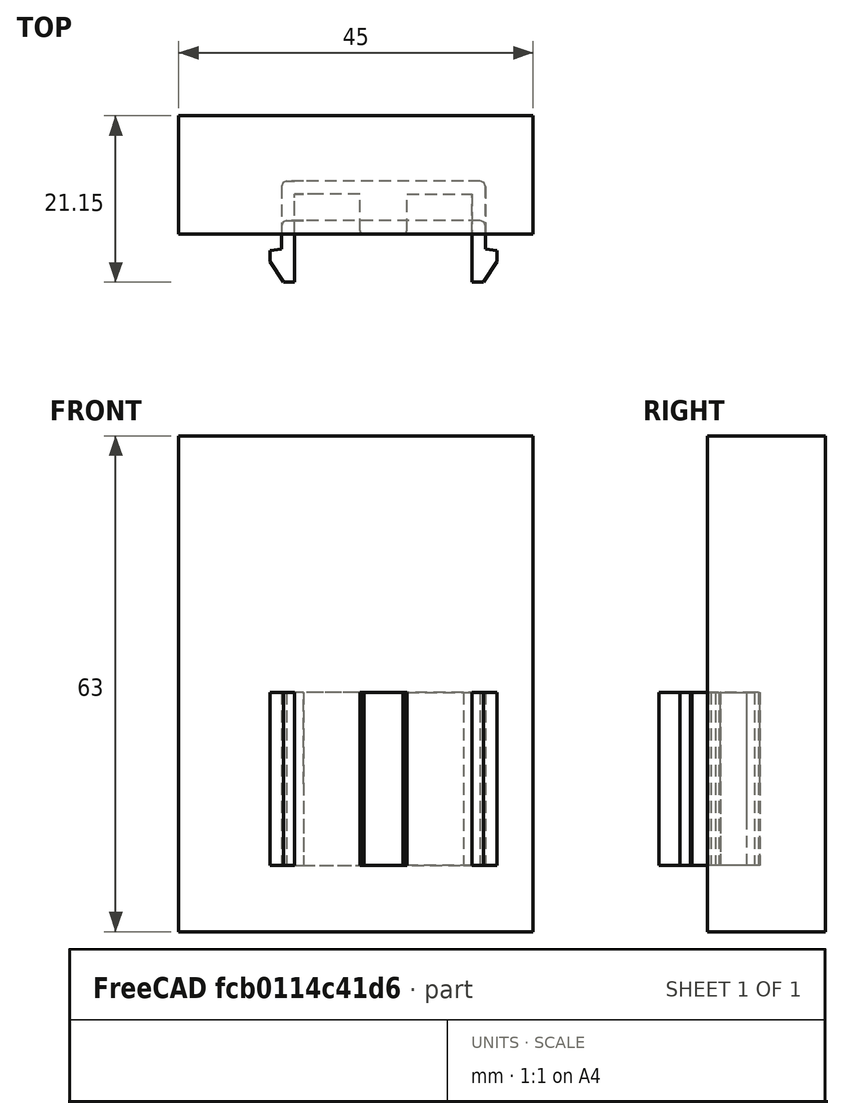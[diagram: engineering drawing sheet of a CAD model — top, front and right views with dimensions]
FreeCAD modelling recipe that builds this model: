
FCSTD DOCUMENT  (FreeCAD 0.17R13541 (Git))
Label: final-extrusion-center-mounter
License: All rights reserved
LicenseURL: http://en.wikipedia.org/wiki/All_rights_reserved
objects: Part::Feature×7, Part::Box×4, Part::MultiCommon×2, Mesh::Feature×1, Part::Cut×1, Part::MultiFuse×1
note: 15 computed .brp shape members not serialized (recipe doc carries the construction recipe); baked Part::Feature solids carry a one-line shape summary decoded from their .brp

FEATURE [Mesh::Feature] cableChain_40MountTop_v2
FEATURE [Part::Feature] cableChain_40MountTop_v2001
  shape: bbox 28.86 x 27.05 x 22 mm, 1492 faces, 0 solids (baked)
FEATURE [Part::Feature] cableChain_40MountTop_v2001_solid  label="cableChain_40MountTop_v2001 (Solid)"
  shape: bbox 28.86 x 27.05 x 22 mm, 1492 faces (baked)
FEATURE [Part::Box] Box  label="Cube"
  AttacherType = Attacher::AttachEngine3D
  Height = 33
  Length = 59
  Placement = pos=(-165.7,-23.2,-95.1) rot=(0,0,1;0rad)
  Width = 31
FEATURE [Part::Feature] cableChain_40MountTop_v2001_solid001  label="cableChain_40MountTop_v2001 (Solid)001"
  shape: bbox 28.86 x 27.05 x 22 mm, 229 faces (baked)
FEATURE [Part::Cut] Cut
  Base = -> cableChain_40MountTop_v2001_solid001
  Tool = -> Box
FEATURE [Part::Box] Box001  label="Cube001"
  AttacherType = Attacher::AttachEngine3D
  Height = 63
  Length = 45
  Placement = pos=(-171,-29.9,-98.4) rot=(0,0,1;0rad)
  Width = 15
FEATURE [Part::Feature] Cut_solid  label="Cut (Solid)"
  shape: bbox 28.86 x 15.02 x 22 mm, 47 faces (baked)
FEATURE [Part::Feature] Cut_solid001  label="Cut (Solid)001"
  shape: bbox 28.86 x 15.02 x 22 mm, 47 faces (baked)
FEATURE [Part::Box] Box002  label="Cube002"
  AttacherType = Attacher::AttachEngine3D
  Height = 63
  Length = 45
  Placement = pos=(-171,-36.9,-98.4) rot=(0,0,1;0rad)
  Width = 7
FEATURE [Part::Box] Box003  label="Cube003"
  AttacherType = Attacher::AttachEngine3D
  Height = 63
  Length = 45
  Placement = pos=(-171,-24.9,-98.4) rot=(0,0,1;0rad)
  Width = 5
FEATURE [Part::MultiCommon] Common
  Placement = pos=(0,-5,0) rot=(0,0,1;0rad)
  Shapes = -> [Box003,Cut_solid001]
FEATURE [Part::MultiCommon] Common001
  Shapes = -> [Cut_solid,Box002]
FEATURE [Part::MultiFuse] Fusion
  Shapes = -> [Common,Common001]
FEATURE [Part::Feature] Fusion001
  shape: bbox 28.86 x 7.85 x 22 mm, 47 faces (baked)
FEATURE [Part::Feature] Fusion_solid  label="Fusion (Solid)"
  shape: bbox 28.86 x 7.85 x 22 mm, 56 faces (baked)
